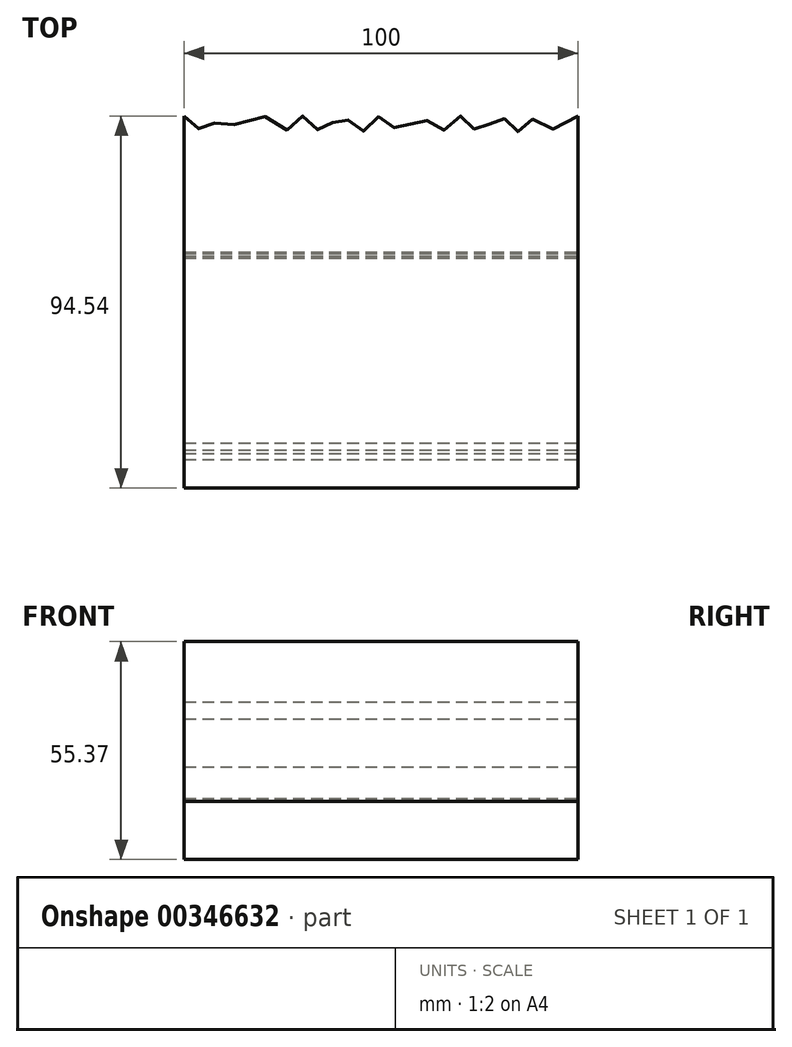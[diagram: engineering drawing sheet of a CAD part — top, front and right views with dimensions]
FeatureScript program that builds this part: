
annotation { "Feature Type Name" : "Feature", "Feature Type Description" : "" }
export const myFeature = defineFeature(function(context is Context, id is Id, definition is map)
    precondition{}
    {
        {
            var Q0;
            Q0=qCreatedBy(makeId("Right.planeOp"),FACE);
            var sketch = newSketch(context, id + "F0", { "sketchPlane" : qUnion([Q0])});
            skLineSegment(sketch, "E0", {"start": v(-84.88, -31.47) * mm, "end": v(-82.3, -46.24) * mm, "construction": true});
            skLineSegment(sketch, "E1", {"start": v(-83.95, -46.49) * mm, "end": v(-87.24, -46.98) * mm});
            skLineSegment(sketch, "E2", {"start": v(-87.24, -46.98) * mm, "end": v(-94.54, -32.18) * mm});
            skArc(sketch, "E3", {"start": v(-7, -7) * mm, "mid": v(-0.06, -0.9) * mm, "end": v(-5.2, 6.76) * mm});
            skArc(sketch, "E4", {"start": v(-5.2, 6.76) * mm, "mid": v(-22.59, 8.14) * mm, "end": v(-39.33, 3.26) * mm});
            skLineSegment(sketch, "E5", {"start": v(-35, -11.31) * mm, "end": v(-33.87, -23.26) * mm, "construction": true});
            skArc(sketch, "E6", {"start": v(-84.88, -31.47) * mm, "mid": v(-85.69, -38.4) * mm, "end": v(-83.27, -44.94) * mm});
            skArc(sketch, "E7", {"start": v(-35, -11.31) * mm, "mid": v(-36.08, -16.65) * mm, "end": v(-34.7, -21.92) * mm});
            skPoint(sketch, "E8.visualSharp", {"position": v(-33.87, -23.26) * mm});
            skArc(sketch, "E8.filletArc", {"start": v(-35.56, -23.39) * mm, "mid": v(-34.72, -22.9) * mm, "end": v(-34.7, -21.92) * mm});
            skPoint(sketch, "E9.visualSharp", {"position": v(-82.3, -46.24) * mm});
            skArc(sketch, "E9.filletArc", {"start": v(-83.95, -46.49) * mm, "mid": v(-83.18, -45.9) * mm, "end": v(-83.27, -44.94) * mm});
            skArc(sketch, "E10", {"start": v(-39.33, 3.26) * mm, "mid": v(-61.54, -8.78) * mm, "end": v(-82.92, -22.22) * mm});
            skLineSegment(sketch, "E11", {"start": v(-7, 0) * mm, "end": v(-35, -11.31) * mm, "construction": true});
            skLineSegment(sketch, "E12", {"start": v(-35, -11.31) * mm, "end": v(-84.88, -31.47) * mm, "construction": true});
            skLineSegment(sketch, "E13", {"start": v(0, 0) * mm, "end": v(-7, 0) * mm, "construction": true});
            skArc(sketch, "E14", {"start": v(-82.92, -22.22) * mm, "mid": v(-89.02, -26.86) * mm, "end": v(-94.54, -32.18) * mm});
            skPoint(sketch, "E15.orphan", {"position": v(-95.2, -30.84) * mm});
            skLineSegment(sketch, "E16", {"start": v(-82.92, -22.22) * mm, "end": v(-95.2, -30.84) * mm, "construction": true});
            skLineSegment(sketch, "E17", {"start": v(-95.2, -30.84) * mm, "end": v(-94.54, -32.18) * mm, "construction": true});
            skLineSegment(sketch, "E18", {"start": v(-84.88, -31.47) * mm, "end": v(-93.23, -34.84) * mm, "construction": true});
            skLineSegment(sketch, "E19", {"start": v(0, 0) * mm, "end": v(0, 6.76) * mm, "construction": true});
            skArc(sketch, "E20", {"start": v(-7, -7) * mm, "mid": v(-21.17, -8.08) * mm, "end": v(-35, -11.31) * mm});
            skArc(sketch, "E21", {"start": v(-35.56, -23.39) * mm, "mid": v(-60.36, -26.62) * mm, "end": v(-84.88, -31.47) * mm});
            skSolve(sketch);
        }
        {
            var Q0;
            Q0=qCreatedBy(makeId("Right.planeOp"),FACE);
            cPlane(context, id + "F1", {"entities" : qUnion([Q0]), "cplaneType" : CPlaneType.OFFSET, "offset" : 100 * mm, "width" : 150 * mm, "height" : 150 * mm});
        }
        {
            var Q0;
            Q0=qCreatedBy(id+"F1.planeOp",FACE);
            var sketch = newSketch(context, id + "F2", { "sketchPlane" : qUnion([Q0])});
            skLineSegment(sketch, "E22", {"start": v(-84.88, -31.47) * mm, "end": v(-82.3, -46.24) * mm, "construction": true});
            skLineSegment(sketch, "E23", {"start": v(-83.95, -46.49) * mm, "end": v(-87.24, -46.98) * mm});
            skLineSegment(sketch, "E24", {"start": v(-87.24, -46.98) * mm, "end": v(-94.54, -32.18) * mm});
            skArc(sketch, "E25", {"start": v(-7, -7) * mm, "mid": v(-0.06, -0.9) * mm, "end": v(-5.2, 6.76) * mm});
            skArc(sketch, "E26", {"start": v(-5.2, 6.76) * mm, "mid": v(-22.59, 8.14) * mm, "end": v(-39.33, 3.26) * mm});
            skLineSegment(sketch, "E27", {"start": v(-35, -11.31) * mm, "end": v(-33.87, -23.26) * mm, "construction": true});
            skArc(sketch, "E28", {"start": v(-84.88, -31.47) * mm, "mid": v(-85.69, -38.4) * mm, "end": v(-83.27, -44.94) * mm});
            skArc(sketch, "E29", {"start": v(-35, -11.31) * mm, "mid": v(-36.08, -16.65) * mm, "end": v(-34.7, -21.92) * mm});
            skPoint(sketch, "E30.visualSharp", {"position": v(-33.87, -23.26) * mm});
            skArc(sketch, "E30.filletArc", {"start": v(-35.56, -23.39) * mm, "mid": v(-34.72, -22.9) * mm, "end": v(-34.7, -21.92) * mm});
            skPoint(sketch, "E31.visualSharp", {"position": v(-82.3, -46.24) * mm});
            skArc(sketch, "E31.filletArc", {"start": v(-83.95, -46.49) * mm, "mid": v(-83.18, -45.9) * mm, "end": v(-83.27, -44.94) * mm});
            skArc(sketch, "E32", {"start": v(-39.33, 3.26) * mm, "mid": v(-61.54, -8.78) * mm, "end": v(-82.92, -22.22) * mm});
            skLineSegment(sketch, "E33", {"start": v(-7, 0) * mm, "end": v(-35, -11.31) * mm, "construction": true});
            skLineSegment(sketch, "E34", {"start": v(-35, -11.31) * mm, "end": v(-84.88, -31.47) * mm, "construction": true});
            skLineSegment(sketch, "E35", {"start": v(0, 0) * mm, "end": v(-7, 0) * mm, "construction": true});
            skArc(sketch, "E36", {"start": v(-82.92, -22.22) * mm, "mid": v(-89.02, -26.86) * mm, "end": v(-94.54, -32.18) * mm});
            skPoint(sketch, "E37.orphan", {"position": v(-95.2, -30.84) * mm});
            skLineSegment(sketch, "E38", {"start": v(-82.92, -22.22) * mm, "end": v(-95.2, -30.84) * mm, "construction": true});
            skLineSegment(sketch, "E39", {"start": v(-95.2, -30.84) * mm, "end": v(-94.54, -32.18) * mm, "construction": true});
            skLineSegment(sketch, "E40", {"start": v(-84.88, -31.47) * mm, "end": v(-93.23, -34.84) * mm, "construction": true});
            skLineSegment(sketch, "E41", {"start": v(0, 0) * mm, "end": v(0, 6.76) * mm, "construction": true});
            skArc(sketch, "E42", {"start": v(-7, -7) * mm, "mid": v(-21.17, -8.08) * mm, "end": v(-35, -11.31) * mm});
            skArc(sketch, "E43", {"start": v(-35.56, -23.39) * mm, "mid": v(-60.36, -26.62) * mm, "end": v(-84.88, -31.47) * mm});
            skSolve(sketch);
        }
        {
            var Q0;
            Q0=qCreatedBy(makeId("Top.planeOp"),FACE);
            var sketch = newSketch(context, id + "F3", { "sketchPlane" : qUnion([Q0])});
            skPoint(sketch, "E44", {"position": v(100, 0) * mm});
            skPoint(sketch, "E45", {"position": v(10, 0) * mm});
            skPoint(sketch, "E46", {"position": v(20, 0) * mm});
            skPoint(sketch, "E47", {"position": v(30, 0) * mm});
            skPoint(sketch, "E48", {"position": v(40, 0) * mm});
            skPoint(sketch, "E49", {"position": v(50, 0) * mm});
            skPoint(sketch, "E50", {"position": v(60, 0) * mm});
            skPoint(sketch, "E51", {"position": v(70, 0) * mm});
            skPoint(sketch, "E52", {"position": v(80, 0) * mm});
            skPoint(sketch, "E53", {"position": v(90, 0) * mm});
            skLineSegment(sketch, "E54", {"start": v(0, 0) * mm, "end": v(10, 0) * mm, "construction": true});
            skLineSegment(sketch, "E55", {"start": v(10, 0) * mm, "end": v(20, 0) * mm, "construction": true});
            skLineSegment(sketch, "E56", {"start": v(20, 0) * mm, "end": v(30, 0) * mm, "construction": true});
            skLineSegment(sketch, "E57", {"start": v(30, 0) * mm, "end": v(40, 0) * mm, "construction": true});
            skLineSegment(sketch, "E58", {"start": v(40, 0) * mm, "end": v(50, 0) * mm, "construction": true});
            skLineSegment(sketch, "E59", {"start": v(50, 0) * mm, "end": v(60, 0) * mm, "construction": true});
            skLineSegment(sketch, "E60", {"start": v(60, 0) * mm, "end": v(70, 0) * mm, "construction": true});
            skLineSegment(sketch, "E61", {"start": v(70, 0) * mm, "end": v(80, 0) * mm, "construction": true});
            skLineSegment(sketch, "E62", {"start": v(80, 0) * mm, "end": v(90, 0) * mm, "construction": true});
            skLineSegment(sketch, "E63", {"start": v(90, 0) * mm, "end": v(100, 0) * mm, "construction": true});
            skPoint(sketch, "E64", {"position": v(5, -4) * mm});
            skPoint(sketch, "E64.positionSnap0", {"position": v(5, 0) * mm});
            skPoint(sketch, "E65", {"position": v(15, -4) * mm});
            skPoint(sketch, "E65.positionSnap0", {"position": v(15, 0) * mm});
            skPoint(sketch, "E66", {"position": v(25, -4) * mm});
            skPoint(sketch, "E66.positionSnap0", {"position": v(25, 0) * mm});
            skPoint(sketch, "E67", {"position": v(35, -4) * mm});
            skPoint(sketch, "E67.positionSnap0", {"position": v(35, 0) * mm});
            skPoint(sketch, "E68", {"position": v(45, -4) * mm});
            skPoint(sketch, "E68.positionSnap0", {"position": v(45, 0) * mm});
            skPoint(sketch, "E69", {"position": v(55, -4) * mm});
            skPoint(sketch, "E69.positionSnap0", {"position": v(55, 0) * mm});
            skPoint(sketch, "E70", {"position": v(65, -4) * mm});
            skPoint(sketch, "E70.positionSnap0", {"position": v(65, 0) * mm});
            skPoint(sketch, "E71", {"position": v(75, -4) * mm});
            skPoint(sketch, "E71.positionSnap0", {"position": v(75, 0) * mm});
            skPoint(sketch, "E72", {"position": v(85, -4) * mm});
            skPoint(sketch, "E72.positionSnap0", {"position": v(85, 0) * mm});
            skPoint(sketch, "E73", {"position": v(95, -4) * mm});
            skPoint(sketch, "E73.positionSnap0", {"position": v(95, 0) * mm});
            skFitSpline(sketch, "E74", {"points": [v(0, 0) * mm, v(5, -4) * mm, v(10, 0) * mm, v(15, -4) * mm, v(20, 0) * mm, v(25, -4) * mm, v(30, 0) * mm, v(35, -4) * mm, v(40, 0) * mm, v(45, -4) * mm, v(50, 0) * mm, v(55, -4) * mm, v(60, 0) * mm, v(65, -4) * mm, v(70, 0) * mm, v(75, -4) * mm, v(80, 0) * mm, v(85, -4) * mm, v(90, 0) * mm, v(95, -4) * mm, v(100, 0) * mm], "startDerivative": vector(100, 0) * mm, "endDerivative": vector(100, 0) * mm});
            skPoint(sketch, "E75", {"position": v(97.5, -2) * mm});
            skPoint(sketch, "E76", {"position": v(92.5, -2) * mm});
            skPoint(sketch, "E77", {"position": v(87.5, -2) * mm});
            skPoint(sketch, "E78", {"position": v(82.5, -2) * mm});
            skPoint(sketch, "E79", {"position": v(77.5, -2) * mm});
            skPoint(sketch, "E80", {"position": v(72.5, -2) * mm});
            skPoint(sketch, "E81", {"position": v(67.5, -2) * mm});
            skPoint(sketch, "E82", {"position": v(62.5, -2) * mm});
            skPoint(sketch, "E83", {"position": v(57.5, -2) * mm});
            skPoint(sketch, "E84", {"position": v(52.5, -2) * mm});
            skPoint(sketch, "E85", {"position": v(47.5, -2) * mm});
            skPoint(sketch, "E86", {"position": v(42.5, -2) * mm});
            skPoint(sketch, "E87", {"position": v(37.5, -2) * mm});
            skPoint(sketch, "E88", {"position": v(32.5, -2) * mm});
            skPoint(sketch, "E89", {"position": v(27.5, -2) * mm});
            skPoint(sketch, "E90", {"position": v(22.5, -2) * mm});
            skPoint(sketch, "E91", {"position": v(17.5, -2) * mm});
            skPoint(sketch, "E92", {"position": v(12.5, -2) * mm});
            skPoint(sketch, "E93", {"position": v(7.5, -2) * mm});
            skPoint(sketch, "E94", {"position": v(2.5, -2) * mm});
            skSolve(sketch);
        }
        {
            var Q0;
            Q0 = qSketchRegion(id + "F0", true);
            var Q1;
            Q1 = qSketchRegion(id + "F2", true);
            var Q2;
            Q2=sQuery(id+"F3.wireOp",EDGE,"E74");
            loft(context, id + "F4", {"addGuides" : true, "sheetProfilesArray" : [{ "sheetProfileEntities" : qUnion([Q0]) }, { "sheetProfileEntities" : qUnion([Q1]) }], "guidesArray" : [{ "guideEntities" : qUnion([Q2]), "guideDerivativeType" : LoftGuideDerivativeType.DEFAULT, "guideDerivativeMagnitude" : 1 }]});
        }
    });
